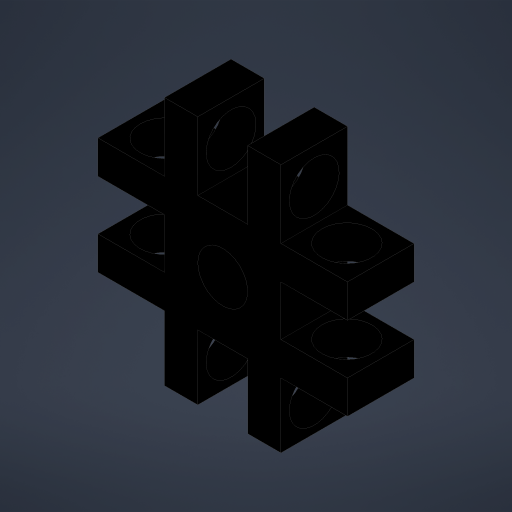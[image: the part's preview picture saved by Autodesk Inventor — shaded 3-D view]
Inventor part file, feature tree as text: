
AUTODESK INVENTOR PART (.ipt)
format: ipt  version: 2023 (Build 270158000, 158)  size: 235,520 bytes
history: native  units: mm
features: extrude x2, sketch x2, pattern_circular x1
ambient origin geometry x8: Origin, YZ Plane, XZ Plane, XY Plane, X Axis, Y Axis, Z Axis, Center Point
bodies: Solid1 (feature_tree)
feature tree (5):
  extrude  "Extrusion1"  Depth=15.0mm
  extrude  "Extrusion2"  Depth=1.5mm
  pattern_circular  "Circular Pattern1"  Angle=90.0deg  [1 undecoded]
  sketch  "Sketch1"  dims[d0=15.0mm d1=15.0mm]
  sketch  "Sketch2"  dims[d2=1.5mm d3=1.5mm d4=90.0deg d5=3.0mm d6=3.0mm d7=2.0mm d8=15.0mm d9=2.0mm d10=2.0mm d11=4.0mm d12=0.0mm d13=3.0mm d14=15.0mm d15=0.0mm d16=40.0mm d17=360.0deg]
note: 1 required parameter value undecoded (feature->parameter linkage not recoverable at this tier; creation-order binding heuristic only, values carry confidence <= 0.55)
